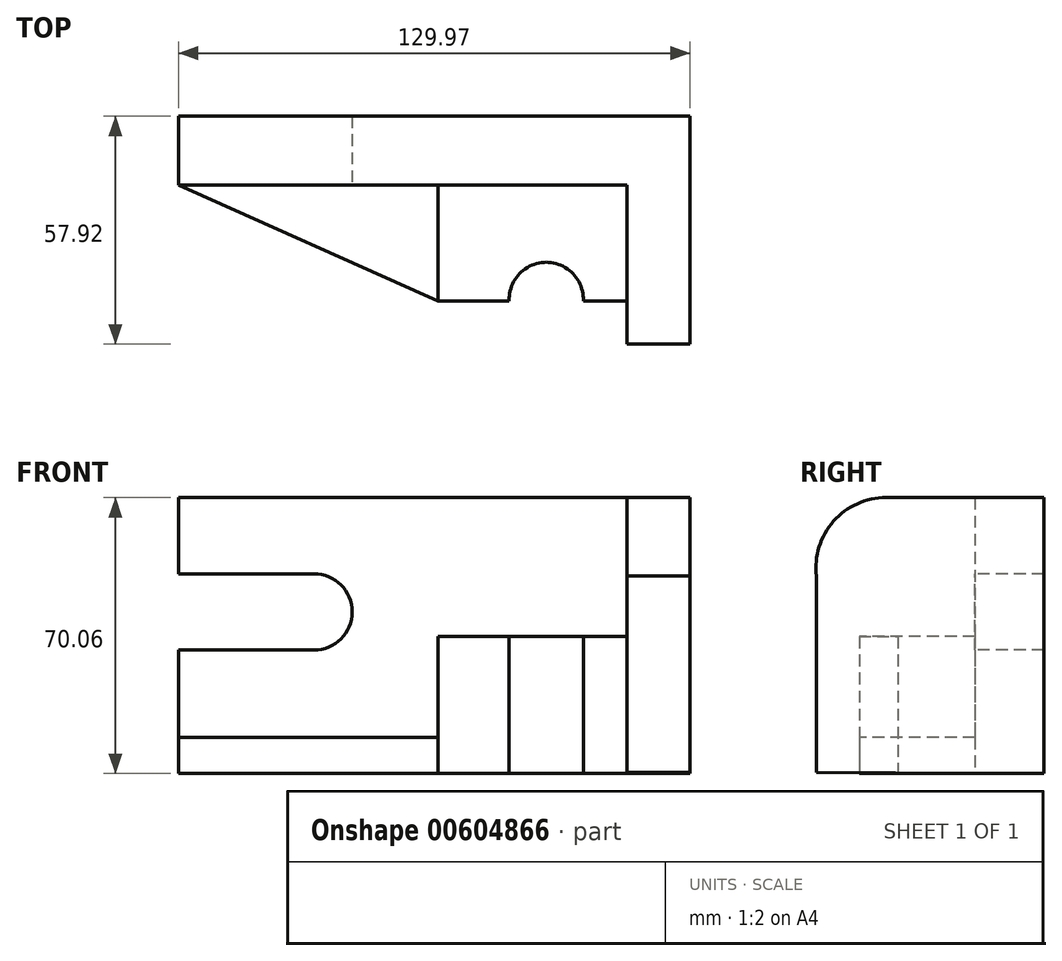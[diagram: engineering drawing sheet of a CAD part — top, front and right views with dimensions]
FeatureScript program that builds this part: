
annotation { "Feature Type Name" : "Feature", "Feature Type Description" : "" }
export const myFeature = defineFeature(function(context is Context, id is Id, definition is map)
    precondition{}
    {
        {
            var Q0;
            Q0=qCreatedBy(makeId("Front.planeOp"),FACE);
            var sketch = newSketch(context, id + "F0", { "sketchPlane" : qUnion([Q0])});
            skLineSegment(sketch, "E0.bottom", {"start": v(-65.9, 34.2) * mm, "end": v(64.06, 34.2) * mm});
            skLineSegment(sketch, "E0.top", {"start": v(-65.9, -35.86) * mm, "end": v(64.06, -35.86) * mm});
            skLineSegment(sketch, "E0.left", {"start": v(-65.9, 34.2) * mm, "end": v(-65.9, -35.86) * mm});
            skLineSegment(sketch, "E0.right", {"start": v(64.06, 34.2) * mm, "end": v(64.06, -35.86) * mm});
            skSolve(sketch);
        }
        {
            var Q0;
            Q0 = qSketchRegion(id + "F0", true);
            extrude(context, id + "F1", {"entities" : qUnion([Q0]), "depth" : 17.53 * mm, "offsetDistance" : 25.4 * mm});
        }
        {
            var Q0;
            Q0=makeQuery(id+"F1.opExtrude","SWEPT_FACE",FACE,{"disambiguationData":[OSD([sQuery(id+"F0.wireOp",EDGE,"E0.right")])]});
            var sketch = newSketch(context, id + "F2", { "sketchPlane" : qUnion([Q0])});
            skLineSegment(sketch, "E1", {"start": v(0, 34.2) * mm, "end": v(-40.1, 34.2) * mm});
            skArc(sketch, "E2", {"start": v(-40.1, 34.2) * mm, "mid": v(-53.42, 28.22) * mm, "end": v(-57.8, 14.29) * mm});
            skLineSegment(sketch, "E3", {"start": v(-57.8, 14.29) * mm, "end": v(-57.8, -35.67) * mm});
            skLineSegment(sketch, "E4", {"start": v(-57.8, -35.67) * mm, "end": v(-15.76, -35.86) * mm});
            skSolve(sketch);
        }
        {
            var Q0;
            {var subQ4=sQuery(id+"F2.wireOp",EDGE,"E2");Q0=makeQuery(id+"F2.imprint","IMPRINT",FACE,{"disambiguationData":[TD([[makeQuery(id+"F2.imprint","IMPRINT",EDGE,{"derivedFrom":subQ4}),1.0]])]});}
            extrude(context, id + "F3", {"entities" : qUnion([Q0]), "operationType" : NewBodyOperationType.ADD, "oppositeDirection" : true, "depth" : 16 * mm, "offsetDistance" : 25.4 * mm});
        }
        {
            var Q0;
            Q0=makeQuery(id+"F1.opExtrude","SWEPT_FACE",FACE,{"disambiguationData":[OSD([sQuery(id+"F0.wireOp",EDGE,"E0.top")])]});
            var sketch = newSketch(context, id + "F4", { "sketchPlane" : qUnion([Q0])});
            skLineSegment(sketch, "E5.bottom", {"start": v(48.06, 17.53) * mm, "end": v(0, 17.53) * mm});
            skLineSegment(sketch, "E5.top", {"start": v(48.06, 46.92) * mm, "end": v(0, 46.92) * mm});
            skLineSegment(sketch, "E5.left", {"start": v(48.06, 17.53) * mm, "end": v(48.06, 46.92) * mm});
            skLineSegment(sketch, "E5.right", {"start": v(0, 17.53) * mm, "end": v(0, 46.92) * mm});
            skSolve(sketch);
        }
        {
            var Q0;
            Q0 = qSketchRegion(id + "F4", true);
            extrude(context, id + "F5", {"entities" : qUnion([Q0]), "operationType" : NewBodyOperationType.ADD, "oppositeDirection" : true, "depth" : 34.8 * mm, "offsetDistance" : 25.4 * mm});
        }
        {
            var Q0;
            Q0=makeQuery(id+"F5.boolean.opBoolean","MERGE",FACE,{"derivedFrom":[makeQuery(id+"F1.opExtrude","SWEPT_FACE",FACE,{"disambiguationData":[OSD([sQuery(id+"F0.wireOp",EDGE,"E0.top")])]}),makeQuery(id+"F5.opExtrude","CAP_FACE",FACE,{"disambiguationData":[OSD([sQuery(id+"F4.wireOp",EDGE,"E5.bottom"),sQuery(id+"F4.wireOp",EDGE,"E5.top"),sQuery(id+"F4.wireOp",EDGE,"E5.left"),sQuery(id+"F4.wireOp",EDGE,"E5.right")])],"isStart":true})]});
            var sketch = newSketch(context, id + "F6", { "sketchPlane" : qUnion([Q0])});
            skCircle(sketch, "E6", {"center": v(24.03, 46.92) * mm, "radius": 13.2 * mm});
            skSolve(sketch);
        }
        {
            var Q0;
            {var subQ0=sQuery(id+"F6.wireOp",EDGE,"E6");var subQ1=makeQuery(id+"F5.opExtrude","CAP_EDGE",EDGE,{"disambiguationData":[OSD([sQuery(id+"F4.wireOp",EDGE,"E5.top")])],"isStart":true});var subQ2=makeQuery(id+"F6.imprint","INTERSECT",VERTEX,{"disambiguationData":[OD(0.0)],"derivedFrom":[subQ1,subQ0]});Q0=makeQuery(id+"F6.imprint","IMPRINT",FACE,{"disambiguationData":[TD([[makeQuery(id+"F6.imprint","IMPRINT",EDGE,{"disambiguationData":[TD([[subQ2,-1.0]])],"derivedFrom":subQ0}),1.0]])]});}
            extrude(context, id + "F7", {"entities" : qUnion([Q0]), "operationType" : NewBodyOperationType.REMOVE, "oppositeDirection" : true, "depth" : 25.4 * mm, "offsetDistance" : 25.4 * mm});
        }
        {
            var Q0;
            Q0=makeQuery(id+"F5.boolean.opBoolean","MERGE",FACE,{"derivedFrom":[makeQuery(id+"F1.opExtrude","SWEPT_FACE",FACE,{"disambiguationData":[OSD([sQuery(id+"F0.wireOp",EDGE,"E0.top")])]}),makeQuery(id+"F5.opExtrude","CAP_FACE",FACE,{"disambiguationData":[OSD([sQuery(id+"F4.wireOp",EDGE,"E5.bottom"),sQuery(id+"F4.wireOp",EDGE,"E5.top"),sQuery(id+"F4.wireOp",EDGE,"E5.left"),sQuery(id+"F4.wireOp",EDGE,"E5.right")])],"isStart":true})]});
            var sketch = newSketch(context, id + "F8", { "sketchPlane" : qUnion([Q0])});
            skArc(sketch, "E7", {"start": v(18.16, 46.92) * mm, "mid": v(27.56, 37.13) * mm, "end": v(36.96, 46.92) * mm});
            skSolve(sketch);
        }
        {
            var Q0;
            Q0 = qSketchRegion(id + "F8", true);
            var Q1;
            {var subQ0=sQuery(id+"F8.wireOp",EDGE,"E7");Q1=makeQuery(id+"F8.imprint","IMPRINT",FACE,{"disambiguationData":[TD([[makeQuery(id+"F8.imprint","IMPRINT",EDGE,{"derivedFrom":subQ0}),1.0]])]});}
            extrude(context, id + "F9", {"entities" : qUnion([Q0, Q1]), "operationType" : NewBodyOperationType.REMOVE, "oppositeDirection" : true, "depth" : 66.3 * mm, "offsetDistance" : 25.4 * mm});
        }
        {
            var Q0;
            Q0=makeQuery(id+"F5.boolean.opBoolean","MERGE",FACE,{"derivedFrom":[makeQuery(id+"F1.opExtrude","SWEPT_FACE",FACE,{"disambiguationData":[OSD([sQuery(id+"F0.wireOp",EDGE,"E0.top")])]}),makeQuery(id+"F5.opExtrude","CAP_FACE",FACE,{"disambiguationData":[OSD([sQuery(id+"F4.wireOp",EDGE,"E5.bottom"),sQuery(id+"F4.wireOp",EDGE,"E5.top"),sQuery(id+"F4.wireOp",EDGE,"E5.left"),sQuery(id+"F4.wireOp",EDGE,"E5.right")])],"isStart":true})]});
            var sketch = newSketch(context, id + "F10", { "sketchPlane" : qUnion([Q0])});
            skLineSegment(sketch, "E8", {"start": v(0, 46.92) * mm, "end": v(-65.9, 17.53) * mm});
            skLineSegment(sketch, "E9", {"start": v(-65.9, 17.53) * mm, "end": v(0, 17.53) * mm});
            skLineSegment(sketch, "E10", {"start": v(0, 17.53) * mm, "end": v(0, 46.92) * mm});
            skSolve(sketch);
        }
        {
            var Q0;
            Q0=makeQuery(id+"F10.imprint","IMPRINT",FACE,{"disambiguationData":[TD([[makeQuery(id+"F10.imprint","IMPRINT",EDGE,{"derivedFrom":sQuery(id+"F10.wireOp",EDGE,"E8")}),1.0]])]});
            extrude(context, id + "F11", {"entities" : qUnion([Q0]), "operationType" : NewBodyOperationType.ADD, "oppositeDirection" : true, "depth" : 9.14 * mm, "offsetDistance" : 25.4 * mm});
        }
        {
            var Q0;
            Q0=makeQuery(id+"F1.opExtrude","CAP_FACE",FACE,{"disambiguationData":[OSD([sQuery(id+"F0.wireOp",EDGE,"E0.bottom"),sQuery(id+"F0.wireOp",EDGE,"E0.top"),sQuery(id+"F0.wireOp",EDGE,"E0.left"),sQuery(id+"F0.wireOp",EDGE,"E0.right")])],"isStart":false});
            var sketch = newSketch(context, id + "F12", { "sketchPlane" : qUnion([Q0])});
            skLineSegment(sketch, "E11", {"start": v(-65.9, 14.84) * mm, "end": v(-31.43, 14.84) * mm});
            skArc(sketch, "E12", {"start": v(-31.43, -4.52) * mm, "mid": v(-21.75, 5.16) * mm, "end": v(-31.43, 14.84) * mm});
            skLineSegment(sketch, "E13", {"start": v(-31.43, -4.52) * mm, "end": v(-65.9, -4.52) * mm});
            skLineSegment(sketch, "E14", {"start": v(-65.9, -4.52) * mm, "end": v(-65.9, 14.84) * mm});
            skSolve(sketch);
        }
        {
            var Q0;
            Q0 = qSketchRegion(id + "F12", true);
            extrude(context, id + "F13", {"entities" : qUnion([Q0]), "operationType" : NewBodyOperationType.REMOVE, "oppositeDirection" : true, "depth" : 99.31 * mm, "offsetDistance" : 25.4 * mm});
        }
    });
